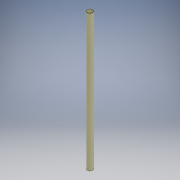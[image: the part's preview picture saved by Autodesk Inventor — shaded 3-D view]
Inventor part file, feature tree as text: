
AUTODESK INVENTOR PART (.ipt)
format: ipt  version: 2018 (Build 220112000, 112)  size: 98,816 bytes
history: native  units: mm
features: chamfer x2, extrude x1, sketch x1
ambient origin geometry x8: Origin, YZ Plane, XZ Plane, XY Plane, X Axis, Y Axis, Z Axis, Center Point
bodies: Solid1 (feature_tree)
feature tree (4):
  extrude  "Extrusion1"  Depth=1000.0mm
  chamfer  "Chamfer1"  Distance=1000.0mm
  chamfer  "Chamfer2"  Distance=1.0mm Angle=45.0deg
  sketch  "Sketch1"  dims[d0=40.0mm d1=2.0mm d2=1000.0mm d3=0.0mm d4=1.0mm d5=2.0mm d6=45.0deg d7=1.0mm d8=2.0mm d9=45.0deg]
